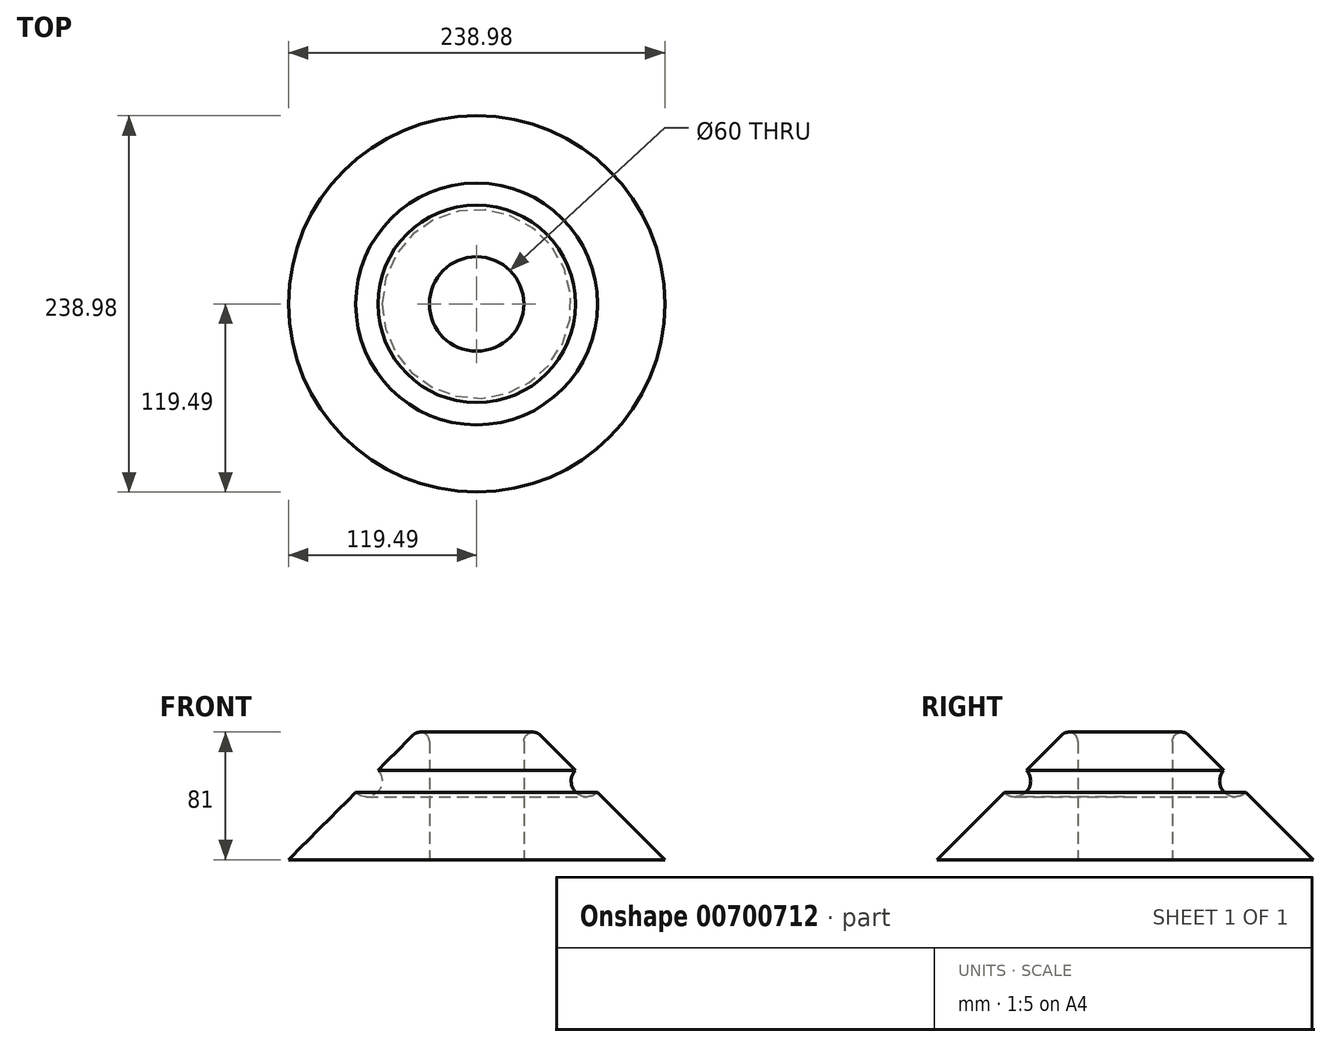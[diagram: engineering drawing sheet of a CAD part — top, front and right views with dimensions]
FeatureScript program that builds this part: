
annotation { "Feature Type Name" : "Feature", "Feature Type Description" : "" }
export const myFeature = defineFeature(function(context is Context, id is Id, definition is map)
    precondition{}
    {
        {
            var Q0;
            Q0=qCreatedBy(makeId("Front.planeOp"),FACE);
            var sketch = newSketch(context, id + "F0", { "sketchPlane" : qUnion([Q0])});
            skLineSegment(sketch, "E0", {"start": v(-30, 0) * mm, "end": v(-30, 75) * mm});
            skLineSegment(sketch, "E1", {"start": v(-40.24, 79.24) * mm, "end": v(-119.49, 0) * mm});
            skLineSegment(sketch, "E2", {"start": v(-119.49, 0) * mm, "end": v(-30, 0) * mm});
            skPoint(sketch, "E3.visualSharp", {"position": v(-30, 89.49) * mm});
            skArc(sketch, "E3.filletArc", {"start": v(-30, 75) * mm, "mid": v(-33.7, 80.54) * mm, "end": v(-40.24, 79.24) * mm});
            skLineSegment(sketch, "E4", {"start": v(0, 0) * mm, "end": v(0, 128.26) * mm, "construction": true});
            skSolve(sketch);
        }
        {
            var Q0;
            Q0=makeQuery(id+"F0.imprint","IMPRINT",FACE,{"disambiguationData":[TD([[makeQuery(id+"F0.imprint","IMPRINT",EDGE,{"derivedFrom":sQuery(id+"F0.wireOp",EDGE,"E0")}),1.0]])]});
            var Q1;
            Q1=sQuery(id+"F0.wireOp",EDGE,"E4");
            revolve(context, id + "F1", {"entities" : qUnion([Q0]), "axis" : qUnion([Q1]), "revolveType" : RevolveType.FULL});
        }
        {
            var Q0;
            Q0=qCreatedBy(makeId("Front.planeOp"),FACE);
            var sketch = newSketch(context, id + "F2", { "sketchPlane" : qUnion([Q0])});
            skCircle(sketch, "E5", {"center": v(-70, 50) * mm, "radius": 10 * mm});
            skLineSegment(sketch, "E6", {"start": v(0, 0) * mm, "end": v(0, 37.85) * mm, "construction": true});
            skSolve(sketch);
        }
        {
            var Q0;
            Q0=makeQuery(id+"F2.imprint","IMPRINT",FACE,{"disambiguationData":[TD([[makeQuery(id+"F2.imprint","IMPRINT",EDGE,{"derivedFrom":sQuery(id+"F2.wireOp",EDGE,"E5")}),1.0]])]});
            var Q1;
            Q1=sQuery(id+"F0.wireOp",EDGE,"E4");
            revolve(context, id + "F3", {"operationType" : NewBodyOperationType.REMOVE, "entities" : qUnion([Q0]), "axis" : qUnion([Q1]), "revolveType" : RevolveType.FULL, "oppositeDirection" : true});
        }
    });
